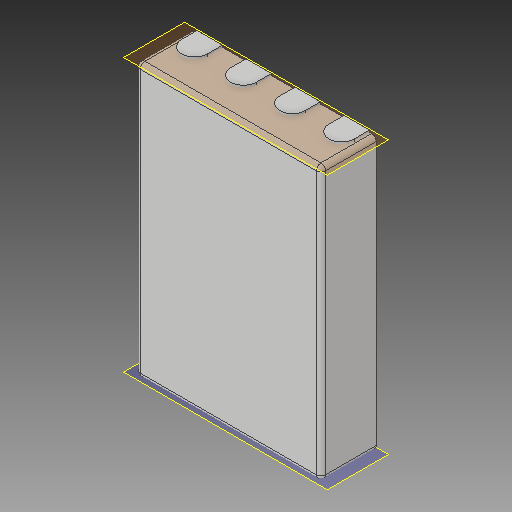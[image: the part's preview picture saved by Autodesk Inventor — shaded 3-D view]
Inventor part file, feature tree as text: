
AUTODESK INVENTOR PART (.ipt)
format: ipt  version: 2019 (Build 230136000, 136)  size: 194,560 bytes
history: native  units: mm
features: other x7, projected_geometry x5, extrude x3, sketch x3, plane x2, fillet x1
ambient origin geometry x8: Origin, YZ Plane, XZ Plane, XY Plane, X Axis, Y Axis, Z Axis, Center Point
bodies: Body1 (feature_tree), Body2 (feature_tree), Body3 (feature_tree)
feature tree (21):
  other  "Sólido1"
  extrude  "Extrusión1"  TaperAngle=90.0deg  [1 undecoded]
  plane  "Plano de trabajo1"
  extrude  "Extrusión2"  Depth=0.3mm TaperAngle=0.0deg
  plane  "Plano de trabajo2"
  extrude  "Extrusión3"  Depth=0.3mm TaperAngle=0.0deg
  fillet  "Empalme1"  Radius=0.05mm
  other  "Edición directa1"
  other  "Edición directa2"
  sketch  "Boceto1"  dims[d0=0.6mm d1=0.0mm d2=90.0deg]
  sketch  "Boceto2"  dims[d3=40.0mm d5=0.53mm d6=10.0mm d8=10.0mm d10=0.3mm d11=0.0mm]
  other  "Sólido2"
  sketch  "Boceto3"  dims[d12=90.0deg d13=0.3mm d14=0.0mm d15=0.05mm d16=0.0mm d17=0.0mm d18=0.02mm d19=0.0mm d20=0.0mm d21=0.02mm]
  projected_geometry  "Contorno proyectado1"
  projected_geometry  "Contorno proyectado2"
  projected_geometry  "Contorno proyectado3"
  projected_geometry  "Contorno proyectado4"
  projected_geometry  "Contorno proyectado5"
  other  "Sólido3"
  other  "Desplazar1"
  other  "Desplazar2"
note: 1 required parameter value undecoded (feature->parameter linkage not recoverable at this tier; creation-order binding heuristic only, values carry confidence <= 0.55)
